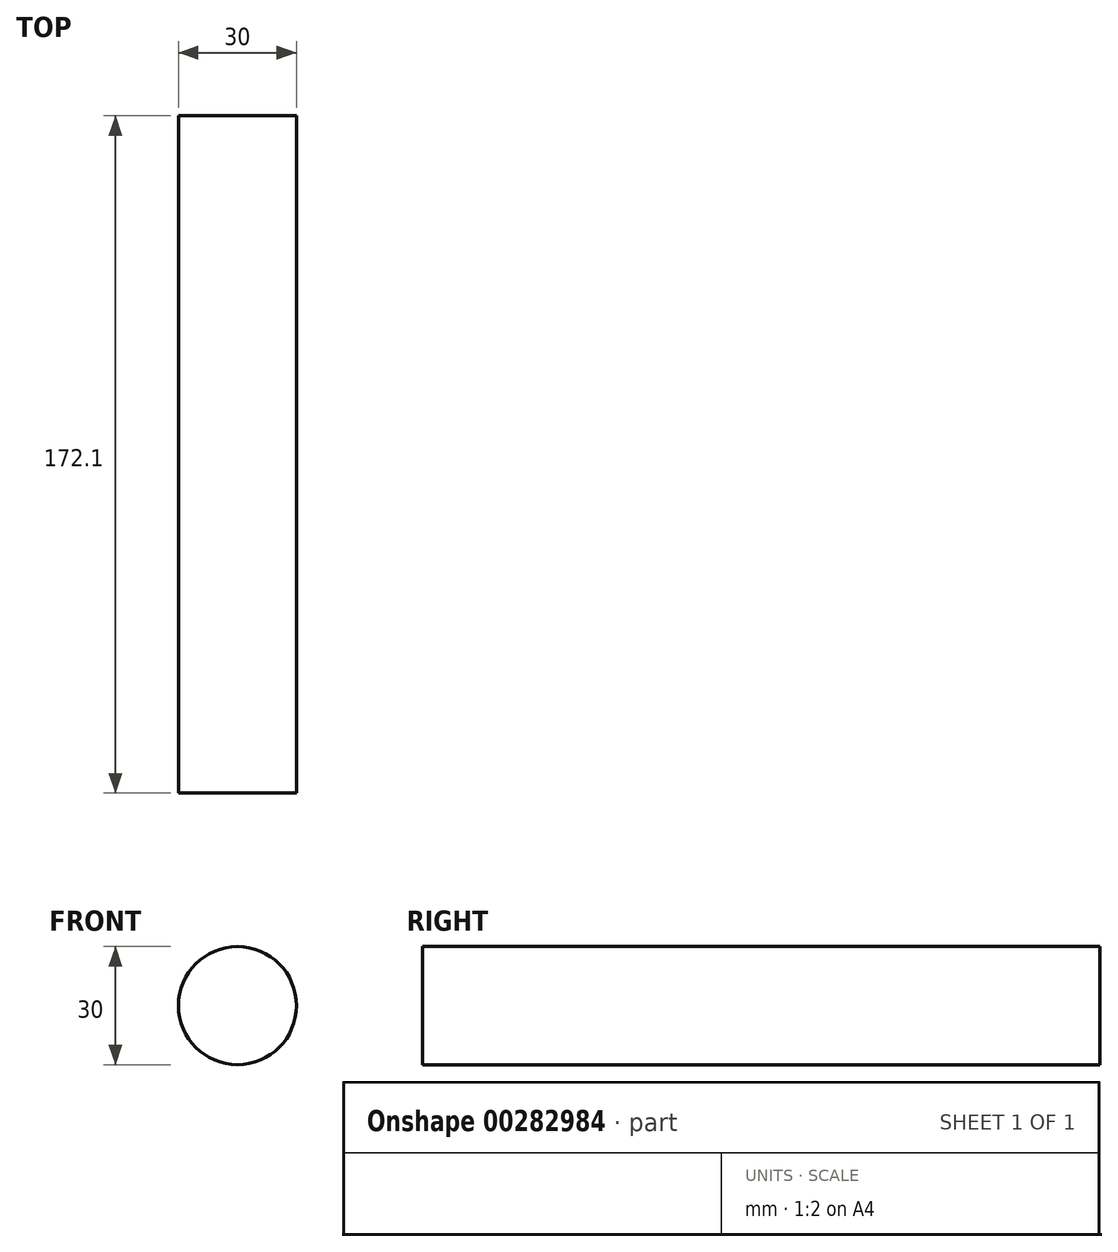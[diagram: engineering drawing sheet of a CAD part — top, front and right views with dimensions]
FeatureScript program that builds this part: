
annotation { "Feature Type Name" : "Feature", "Feature Type Description" : "" }
export const myFeature = defineFeature(function(context is Context, id is Id, definition is map)
    precondition{}
    {
        {
            var Q0;
            Q0=qCreatedBy(makeId("Front.planeOp"),FACE);
            var sketch = newSketch(context, id + "F0", { "sketchPlane" : qUnion([Q0])});
            skCircle(sketch, "E0", {"center": v(0, 0) * mm, "radius": 15 * mm});
            skSolve(sketch);
        }
        {
            var Q0;
            Q0 = qSketchRegion(id + "F0", true);
            extrude(context, id + "F1", {"entities" : qUnion([Q0]), "depth" : 172.1 * mm});
        }
    });
